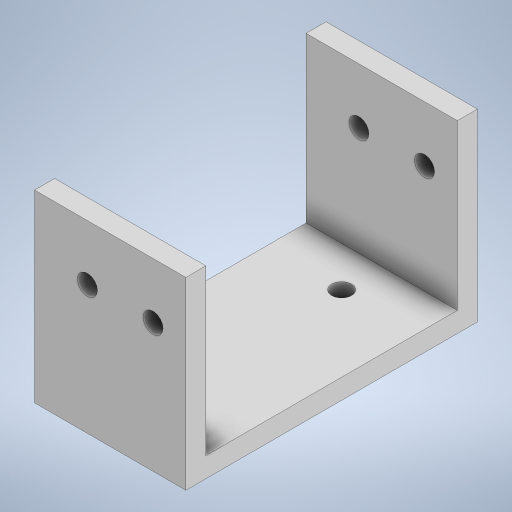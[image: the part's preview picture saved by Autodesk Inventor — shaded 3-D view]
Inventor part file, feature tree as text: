
AUTODESK INVENTOR PART (.ipt)
format: ipt  version: 2023 (Build 270158000, 158)  size: 314,880 bytes
history: native  units: mm
features: extrude x3, sketch x3
ambient origin geometry x8: Origin, YZ Plane, XZ Plane, XY Plane, X Axis, Y Axis, Z Axis, Center Point
bodies: Solid1 (feature_tree)
feature tree (6):
  extrude  "Extrusion1"  Depth=20.0mm
  extrude  "Extrusion2"  Depth=26.0mm
  extrude  "Extrusion3"  Depth=10.0mm
  sketch  "Sketch1"  dims[d0=20.0mm d1=20.0mm]
  sketch  "Sketch2"  dims[d2=55.5mm d3=26.0mm]
  sketch  "Sketch3"  dims[d5=20.0mm d6=45.5mm d7=20.0mm d8=10.0mm d9=10.0mm d10=26.0mm d11=75.5mm d12=0.0mm d13=75.5mm d14=0.0mm d21=65.5mm d22=55.5mm d23=10.0mm d24=10.0mm d25=0.0mm d26=0.0mm]
